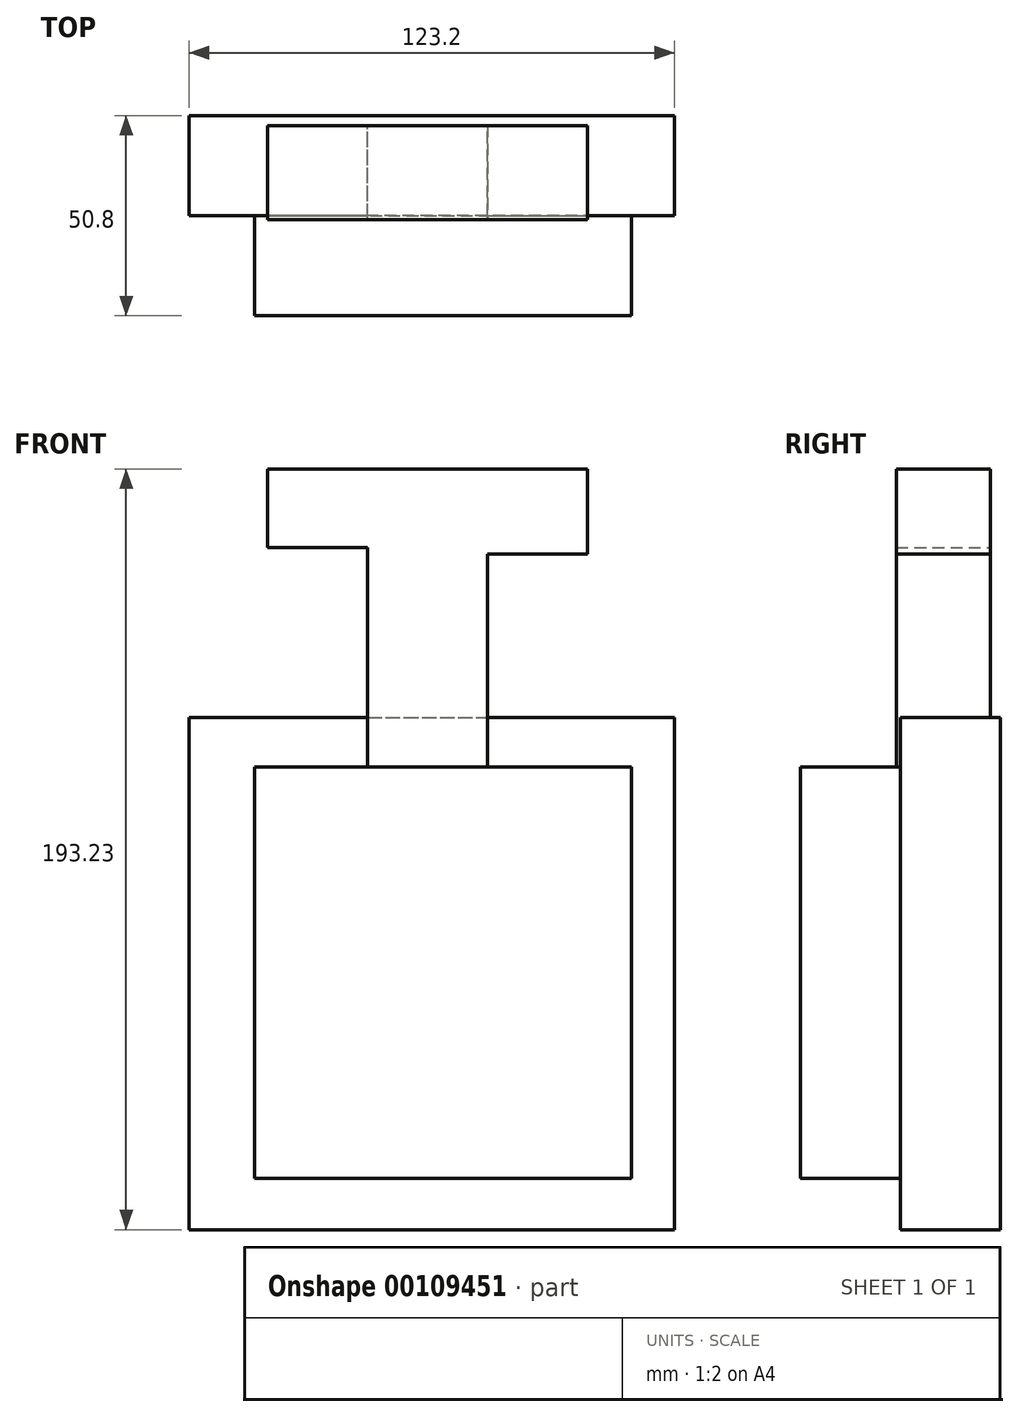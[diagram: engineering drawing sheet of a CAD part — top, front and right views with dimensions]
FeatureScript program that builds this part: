
annotation { "Feature Type Name" : "Feature", "Feature Type Description" : "" }
export const myFeature = defineFeature(function(context is Context, id is Id, definition is map)
    precondition{}
    {
        {
            var Q0;
            Q0=qCreatedBy(makeId("Front.planeOp"),FACE);
            var sketch = newSketch(context, id + "F0", { "sketchPlane" : qUnion([Q0])});
            skLineSegment(sketch, "E0.bottom", {"start": v(-61.24, 63.84) * mm, "end": v(61.96, 63.84) * mm});
            skLineSegment(sketch, "E0.top", {"start": v(-61.24, -66.23) * mm, "end": v(61.96, -66.23) * mm});
            skLineSegment(sketch, "E0.left", {"start": v(-61.24, 63.84) * mm, "end": v(-61.24, -66.23) * mm});
            skLineSegment(sketch, "E0.right", {"start": v(61.96, 63.84) * mm, "end": v(61.96, -66.23) * mm});
            skSolve(sketch);
        }
        {
            var Q0;
            Q0 = qSketchRegion(id + "F0", true);
            extrude(context, id + "F1", {"entities" : qUnion([Q0]), "depth" : 25.4 * mm});
        }
        {
            var Q0;
            Q0=qCreatedBy(makeId("Front.planeOp"),FACE);
            var sketch = newSketch(context, id + "F2", { "sketchPlane" : qUnion([Q0])});
            skLineSegment(sketch, "E1.bottom", {"start": v(-44.69, 51.37) * mm, "end": v(51.12, 51.37) * mm});
            skLineSegment(sketch, "E1.top", {"start": v(-44.69, -53.19) * mm, "end": v(51.12, -53.19) * mm});
            skLineSegment(sketch, "E1.left", {"start": v(-44.69, 51.37) * mm, "end": v(-44.69, -53.19) * mm});
            skLineSegment(sketch, "E1.right", {"start": v(51.12, 51.37) * mm, "end": v(51.12, -53.19) * mm});
            skSolve(sketch);
        }
        {
            var Q0;
            Q0 = qSketchRegion(id + "F2", true);
            extrude(context, id + "F3", {"entities" : qUnion([Q0]), "operationType" : NewBodyOperationType.ADD, "depth" : 50.8 * mm});
        }
        {
            var Q0;
            Q0=qCreatedBy(makeId("Top.planeOp"),FACE);
            var sketch = newSketch(context, id + "F4", { "sketchPlane" : qUnion([Q0])});
            skLineSegment(sketch, "E2.bottom", {"start": v(14.47, -2.49) * mm, "end": v(-15.97, -2.49) * mm});
            skLineSegment(sketch, "E2.top", {"start": v(14.47, -26.37) * mm, "end": v(-15.97, -26.37) * mm});
            skLineSegment(sketch, "E2.left", {"start": v(14.47, -2.49) * mm, "end": v(14.47, -26.37) * mm});
            skLineSegment(sketch, "E2.right", {"start": v(-15.97, -2.49) * mm, "end": v(-15.97, -26.37) * mm});
            skSolve(sketch);
        }
        {
            var Q0;
            Q0 = qSketchRegion(id + "F4", true);
            extrude(context, id + "F5", {"entities" : qUnion([Q0]), "operationType" : NewBodyOperationType.ADD, "depth" : 101.6 * mm});
        }
        {
            var Q0;
            Q0=makeQuery(id+"F5.opExtrude","CAP_FACE",FACE,{"disambiguationData":[OSD([sQuery(id+"F4.wireOp",EDGE,"E2.bottom"),sQuery(id+"F4.wireOp",EDGE,"E2.top"),sQuery(id+"F4.wireOp",EDGE,"E2.left"),sQuery(id+"F4.wireOp",EDGE,"E2.right")])],"isStart":false});
            var sketch = newSketch(context, id + "F6", { "sketchPlane" : qUnion([Q0])});
            skLineSegment(sketch, "E3.bottom", {"start": v(-15.97, -26.37) * mm, "end": v(14.47, -26.37) * mm});
            skLineSegment(sketch, "E3.top", {"start": v(-15.97, -2.49) * mm, "end": v(14.47, -2.49) * mm});
            skLineSegment(sketch, "E3.left", {"start": v(-15.97, -26.37) * mm, "end": v(-15.97, -2.49) * mm});
            skLineSegment(sketch, "E3.right", {"start": v(14.47, -26.37) * mm, "end": v(14.47, -2.49) * mm});
            skSolve(sketch);
        }
        {
            var Q0;
            Q0 = qSketchRegion(id + "F6", true);
            extrude(context, id + "F7", {"entities" : qUnion([Q0]), "operationType" : NewBodyOperationType.ADD, "depth" : 25.4 * mm});
        }
        {
            var Q0;
            Q0=makeQuery(id+"F7.boolean.opBoolean","MERGE",FACE,{"derivedFrom":[makeQuery(id+"F5.opExtrude","SWEPT_FACE",FACE,{"disambiguationData":[OSD([sQuery(id+"F4.wireOp",EDGE,"E2.right")])]}),makeQuery(id+"F7.opExtrude","SWEPT_FACE",FACE,{"disambiguationData":[OSD([sQuery(id+"F6.wireOp",EDGE,"E3.left")])]})]});
            var sketch = newSketch(context, id + "F8", { "sketchPlane" : qUnion([Q0])});
            skLineSegment(sketch, "E4.bottom", {"start": v(26.37, 127) * mm, "end": v(2.49, 127) * mm});
            skLineSegment(sketch, "E4.top", {"start": v(26.37, 107.05) * mm, "end": v(2.49, 107.05) * mm});
            skLineSegment(sketch, "E4.left", {"start": v(26.37, 127) * mm, "end": v(26.37, 107.05) * mm});
            skLineSegment(sketch, "E4.right", {"start": v(2.49, 127) * mm, "end": v(2.49, 107.05) * mm});
            skSolve(sketch);
        }
        {
            var Q0;
            Q0 = qSketchRegion(id + "F8", true);
            extrude(context, id + "F9", {"entities" : qUnion([Q0]), "operationType" : NewBodyOperationType.ADD, "depth" : 25.4 * mm});
        }
        {
            var Q0;
            Q0=makeQuery(id+"F7.boolean.opBoolean","MERGE",FACE,{"derivedFrom":[makeQuery(id+"F5.opExtrude","SWEPT_FACE",FACE,{"disambiguationData":[OSD([sQuery(id+"F4.wireOp",EDGE,"E2.left")])]}),makeQuery(id+"F7.opExtrude","SWEPT_FACE",FACE,{"disambiguationData":[OSD([sQuery(id+"F6.wireOp",EDGE,"E3.right")])]})]});
            var sketch = newSketch(context, id + "F10", { "sketchPlane" : qUnion([Q0])});
            skLineSegment(sketch, "E5.bottom", {"start": v(-2.49, 127) * mm, "end": v(-26.37, 127) * mm});
            skLineSegment(sketch, "E5.top", {"start": v(-2.49, 105.4) * mm, "end": v(-26.37, 105.4) * mm});
            skLineSegment(sketch, "E5.left", {"start": v(-2.49, 127) * mm, "end": v(-2.49, 105.4) * mm});
            skLineSegment(sketch, "E5.right", {"start": v(-26.37, 127) * mm, "end": v(-26.37, 105.4) * mm});
            skSolve(sketch);
        }
        {
            var Q0;
            Q0 = qSketchRegion(id + "F10", true);
            extrude(context, id + "F11", {"entities" : qUnion([Q0]), "operationType" : NewBodyOperationType.ADD, "depth" : 25.4 * mm});
        }
    });
